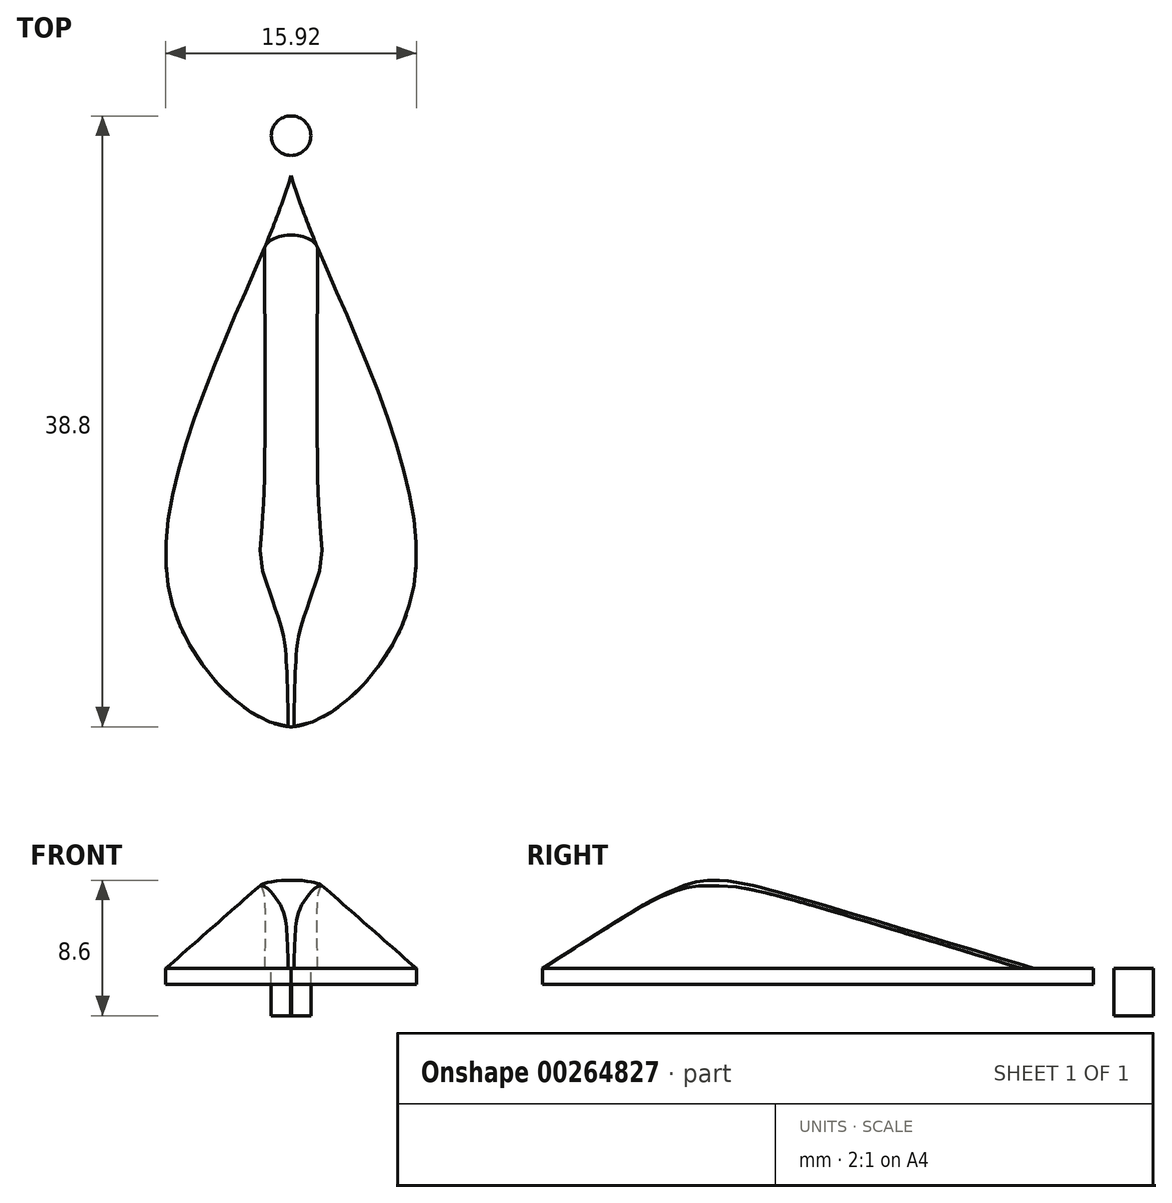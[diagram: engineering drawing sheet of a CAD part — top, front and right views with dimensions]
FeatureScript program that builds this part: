
annotation { "Feature Type Name" : "Feature", "Feature Type Description" : "" }
export const myFeature = defineFeature(function(context is Context, id is Id, definition is map)
    precondition{}
    {
        {
            var Q0;
            Q0=qCreatedBy(makeId("Top.planeOp"),FACE);
            var sketch = newSketch(context, id + "F0", { "sketchPlane" : qUnion([Q0])});
            skLineSegment(sketch, "E0", {"start": v(0, 17.48) * mm, "end": v(0, -17.52) * mm, "construction": true});
            skFitSpline(sketch, "E1", {"points": [v(0, 17.48) * mm, v(-3.83, 7.97) * mm, v(-7.81, -4.46) * mm, v(-6.38, -12.43) * mm, v(0, -17.52) * mm], "startDerivative": vector(-11.03, -36.48) * mm, "endDerivative": vector(32.1, -2.22) * mm});
            skFitSpline(sketch, "E2.MirrorCS", {"points": [v(0, 17.48) * mm, v(3.83, 7.97) * mm, v(7.81, -4.46) * mm, v(6.38, -12.43) * mm, v(0, -17.52) * mm], "startDerivative": vector(11.03, -36.48) * mm, "endDerivative": vector(-32.1, -2.22) * mm});
            skSolve(sketch);
        }
        {
            var Q0;
            Q0=qCreatedBy(makeId("Top.planeOp"),FACE);
            cPlane(context, id + "F1", {"entities" : qUnion([Q0]), "cplaneType" : CPlaneType.OFFSET, "offset" : 7 * mm, "width" : 150 * mm, "height" : 150 * mm});
        }
        {
            var Q0;
            Q0=qCreatedBy(id+"F1.planeOp",FACE);
            var sketch = newSketch(context, id + "F2", { "sketchPlane" : qUnion([Q0])});
            skPoint(sketch, "E3", {"position": v(0, -6.54) * mm});
            skSolve(sketch);
        }
        {
            var Q0;
            Q0=makeQuery(id+"F0.imprint","IMPRINT",FACE,{"disambiguationData":[TD([[makeQuery(id+"F0.imprint","IMPRINT",EDGE,{"derivedFrom":sQuery(id+"F0.wireOp",EDGE,"E1")}),1.0]])]});
            var Q1;
            Q1=sQuery(id+"F2.wireOp",VERTEX,"E3");
            loft(context, id + "F3", {"sheetProfilesArray" : [{ "sheetProfileEntities" : qUnion([Q0]) }, { "sheetProfileEntities" : qUnion([Q1]) }]});
        }
        {
            var Q0;
            {var subQ0=sQuery(id+"F2.wireOp",VERTEX,"E3");var subQ1=sQuery(id+"F0.wireOp",EDGE,"E2.MirrorCS");var subQ2=sQuery(id+"F0.wireOp",EDGE,"E1");Q0=makeQuery(id+"F3.opLoft","SWEPT_EDGE",EDGE,{"disambiguationData":[OSD([subQ2,subQ1,subQ0]),TDD([makeQuery(id+"F0.imprint","INTERSECT",VERTEX,{"disambiguationData":[OD(1.0)],"derivedFrom":[subQ2,subQ1]}),subQ0])]});}
            var Q1;
            {var subQ0=sQuery(id+"F2.wireOp",VERTEX,"E3");var subQ1=sQuery(id+"F0.wireOp",EDGE,"E2.MirrorCS");var subQ2=sQuery(id+"F0.wireOp",EDGE,"E1");Q1=makeQuery(id+"F3.opLoft","SWEPT_EDGE",EDGE,{"disambiguationData":[OSD([subQ2,subQ1,subQ0]),TDD([makeQuery(id+"F0.imprint","INTERSECT",VERTEX,{"disambiguationData":[OD(0.0)],"derivedFrom":[subQ2,subQ1]}),subQ0])]});}
            fillet(context, id + "F4", {"entities" : qUnion([Q0, Q1]), "radius" : 3 * mm, "tangentPropagation" : true, "rho" : .2, "crossSection" : FilletCrossSection.CONIC, "allowEdgeOverflow" : false});
        }
        {
            var Q0;
            Q0=makeQuery(id+"F3.opLoft","CAP_FACE",FACE,{"disambiguationData":[OSD([makeQuery(id+"F0.imprint","IMPRINT",FACE,{"disambiguationData":[TD([[makeQuery(id+"F0.imprint","IMPRINT",EDGE,{"derivedFrom":sQuery(id+"F0.wireOp",EDGE,"E1")}),1.0]])]})])],"isStart":true});
            var sketch = newSketch(context, id + "F5", { "sketchPlane" : qUnion([Q0])});
            skFitSpline(sketch, "E4", {"points": [v(-3.81, -8) * mm, v(0, -17.43) * mm], "startDerivative": vector(3.8, -9.43) * mm, "endDerivative": vector(3.8, -9.43) * mm});
            skFitSpline(sketch, "E5", {"points": [v(0, -17.43) * mm, v(4.02, -7.52) * mm], "startDerivative": vector(4.01, 9.9) * mm, "endDerivative": vector(4.01, 9.9) * mm});
            skSolve(sketch);
        }
        {
            var Q0;
            Q0=makeQuery(id+"F0.imprint","IMPRINT",FACE,{"disambiguationData":[TD([[makeQuery(id+"F0.imprint","IMPRINT",EDGE,{"derivedFrom":sQuery(id+"F0.wireOp",EDGE,"E1")}),1.0]])]});
            var Q1;
            {var subQ0=sQuery(id+"F0.wireOp",EDGE,"E1");var subQ1=makeQuery(id+"F0.imprint","IMPRINT",EDGE,{"derivedFrom":subQ0});var subQ2=sQuery(id+"F0.wireOp",EDGE,"E2.MirrorCS");var subQ4=makeQuery(id+"F3.opLoft","CAP_FACE",FACE,{"disambiguationData":[OSD([makeQuery(id+"F0.imprint","IMPRINT",FACE,{"disambiguationData":[TD([[subQ1,1.0]])]})])],"isStart":true});var subQ5=sQuery(id+"F2.wireOp",VERTEX,"E3");var subQ6=makeQuery(id+"F0.imprint","INTERSECT",VERTEX,{"disambiguationData":[OD(0.0)],"derivedFrom":[subQ0,subQ2]});var subQ7=makeQuery(id+"F3.opLoft","SWEPT_EDGE",EDGE,{"disambiguationData":[OSD([subQ0,subQ2,subQ5]),TDD([subQ6,subQ5])]});var subQ12=makeQuery(id+"F4.opFillet","BLEND_EDGE",EDGE,{"disambiguationData":[OD(0.0)],"blendedFrom":[subQ7,subQ4],"blendedInto":[subQ4]});Q1=makeQuery(id+"F5.imprint","IMPRINT",FACE,{"disambiguationData":[TD([[makeQuery(id+"F5.imprint","IMPRINT",EDGE,{"derivedFrom":subQ12}),1.0]])]});}
            var Q2;
            Q2=makeQuery(id+"F3.opLoft","CAP_FACE",FACE,{"disambiguationData":[OSD([makeQuery(id+"F0.imprint","IMPRINT",FACE,{"disambiguationData":[TD([[makeQuery(id+"F0.imprint","IMPRINT",EDGE,{"derivedFrom":sQuery(id+"F0.wireOp",EDGE,"E1")}),1.0]])]})])],"isStart":true});
            extrude(context, id + "F6", {"entities" : qUnion([Q0, Q1, Q2]), "operationType" : NewBodyOperationType.ADD, "oppositeDirection" : true, "depth" : 1 * mm, "offsetDistance" : 25 * mm});
        }
        {
            var Q0;
            Q0=qCreatedBy(makeId("Top.planeOp"),FACE);
            var sketch = newSketch(context, id + "F7", { "sketchPlane" : qUnion([Q0])});
            skPoint(sketch, "E6", {"position": v(0, -18.8) * mm});
            skFitSpline(sketch, "E7.MirrorCS", {"points": [v(0, 18.8) * mm, v(4.04, 10.43) * mm, v(6.58, 4.4) * mm, v(9, -4.45) * mm, v(7.26, -13.37) * mm, v(0, -18.68) * mm], "startDerivative": vector(20.92, -42.57) * mm, "endDerivative": vector(-50.84, -4.37) * mm});
            skFitSpline(sketch, "E8.MirrorCS", {"points": [v(0, 18.8) * mm, v(-4.04, 10.43) * mm, v(-6.58, 4.4) * mm, v(-9, -4.45) * mm, v(-7.26, -13.37) * mm, v(0, -18.68) * mm], "startDerivative": vector(-20.92, -42.57) * mm, "endDerivative": vector(50.84, -4.37) * mm});
            skEllipse(sketch, "E9.MirrorC", {"center": v(0, -21.54) * mm, "majorRadius": 2.87 * mm, "minorRadius": 1.62 * mm, "majorAxis": v(0, 1)});
            skCircle(sketch, "E10.MirrorC", {"center": v(0, 20.03) * mm, "radius": 1.26 * mm});
            skSolve(sketch);
        }
        {
            var Q0;
            {var subQ1=sQuery(id+"F7.wireOp",EDGE,"E7.MirrorCS");var subQ3=sQuery(id+"F7.wireOp",EDGE,"E10.MirrorC");var subQ4=makeQuery(id+"F7.imprint","INTERSECT",VERTEX,{"derivedFrom":[subQ1,subQ3]});Q0=makeQuery(id+"F7.imprint","IMPRINT",FACE,{"disambiguationData":[TD([[makeQuery(id+"F7.imprint","IMPRINT",EDGE,{"disambiguationData":[TD([[subQ4,-1.0]])],"derivedFrom":subQ3}),1.0]])]});}
            extrude(context, id + "F8", {"entities" : qUnion([Q0]), "operationType" : NewBodyOperationType.ADD, "oppositeDirection" : true, "depth" : 3 * mm, "offsetDistance" : 25 * mm});
        }
    });
